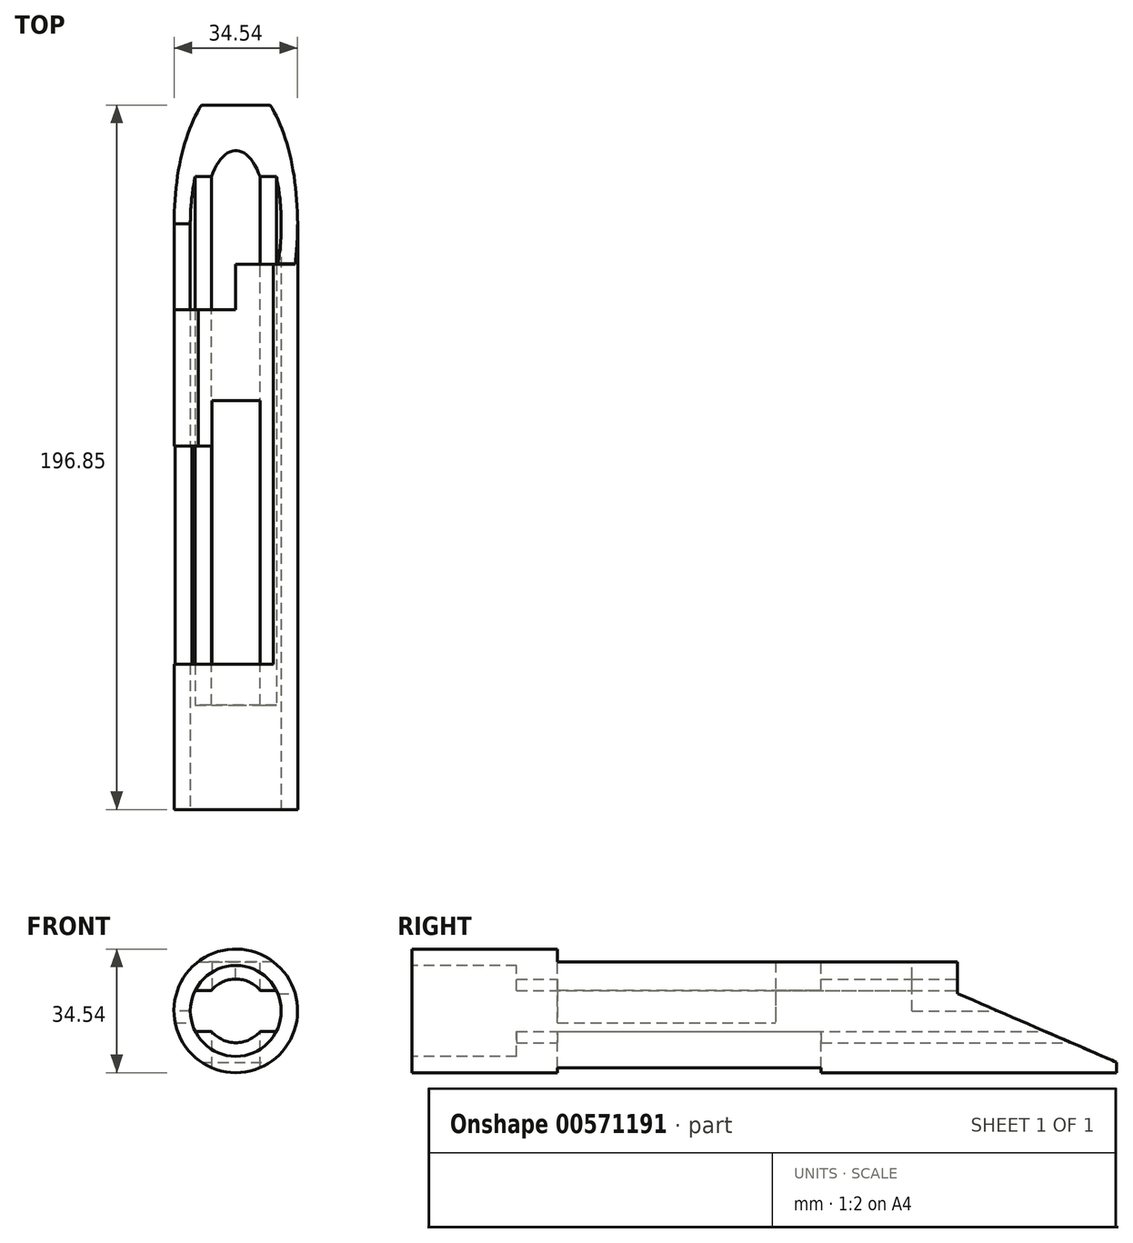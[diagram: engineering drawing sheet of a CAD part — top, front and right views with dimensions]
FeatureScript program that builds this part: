
annotation { "Feature Type Name" : "Feature", "Feature Type Description" : "" }
export const myFeature = defineFeature(function(context is Context, id is Id, definition is map)
    precondition{}
    {
        {
            var Q0;
            Q0=qCreatedBy(makeId("Front.planeOp"),FACE);
            var sketch = newSketch(context, id + "F0", { "sketchPlane" : qUnion([Q0])});
            skCircle(sketch, "E0", {"center": v(0, 0) * mm, "radius": 17.27 * mm});
            skCircle(sketch, "E1", {"center": v(0, 0) * mm, "radius": 8.89 * mm});
            skSolve(sketch);
        }
        {
            var Q0;
            Q0=qSketchRegion(id+"F0",true);
            extrude(context, id + "F1", {"entities" : qUnion([Q0]), "depth" : 196.85 * mm});
        }
        {
            var Q0;
            Q0=makeQuery(id+"F1.opExtrude","CAP_FACE",FACE,{"disambiguationData":[OSD([sQuery(id+"F0.wireOp",EDGE,"E0"),sQuery(id+"F0.wireOp",EDGE,"E1")])],"isStart":false});
            var sketch = newSketch(context, id + "F2", { "sketchPlane" : qUnion([Q0])});
            skCircle(sketch, "E2", {"center": v(0, 0) * mm, "radius": 12.7 * mm});
            skSolve(sketch);
        }
        {
            var Q0;
            Q0=qSketchRegion(id+"F2",true);
            extrude(context, id + "F3", {"entities" : qUnion([Q0]), "operationType" : NewBodyOperationType.REMOVE, "oppositeDirection" : true, "depth" : 29.2 * mm});
        }
        {
            var Q0;
            Q0=makeQuery(id+"F1.opExtrude","CAP_FACE",FACE,{"disambiguationData":[OSD([sQuery(id+"F0.wireOp",EDGE,"E0"),sQuery(id+"F0.wireOp",EDGE,"E1")])],"isStart":false});
            var sketch = newSketch(context, id + "F4", { "sketchPlane" : qUnion([Q0])});
            skArc(sketch, "E3", {"start": v(-11.34, 5.71) * mm, "mid": v(-12.7, 0) * mm, "end": v(-11.34, -5.71) * mm});
            skLineSegment(sketch, "E4", {"start": v(-11.34, 5.72) * mm, "end": v(11.34, 5.72) * mm});
            skLineSegment(sketch, "E5", {"start": v(-11.34, -5.72) * mm, "end": v(11.34, -5.72) * mm});
            skArc(sketch, "E6.trimOffspring", {"start": v(11.34, -5.71) * mm, "mid": v(12.7, 0) * mm, "end": v(11.34, 5.72) * mm});
            skSolve(sketch);
        }
        {
            var Q0;
            Q0=qSketchRegion(id+"F4",true);
            extrude(context, id + "F5", {"entities" : qUnion([Q0]), "operationType" : NewBodyOperationType.REMOVE, "endBound" : BoundingType.THROUGH_ALL, "oppositeDirection" : true, "depth" : 25.4 * mm});
        }
        {
            var Q0;
            Q0=qCreatedBy(makeId("Right.planeOp"),FACE);
            var sketch = newSketch(context, id + "F6", { "sketchPlane" : qUnion([Q0])});
            skLineSegment(sketch, "E7.bottom", {"start": v(-156.21, 26.76) * mm, "end": v(57.64, 26.76) * mm});
            skLineSegment(sketch, "E7.top", {"start": v(-156.21, 13.72) * mm, "end": v(57.64, 13.72) * mm});
            skLineSegment(sketch, "E7.left", {"start": v(-156.21, 26.76) * mm, "end": v(-156.21, 13.72) * mm});
            skLineSegment(sketch, "E7.right", {"start": v(57.64, 26.76) * mm, "end": v(57.64, 13.72) * mm});
            skSolve(sketch);
        }
        {
            var Q0;
            Q0=makeQuery(id+"F6.imprint","IMPRINT",FACE,{"disambiguationData":[TD([[makeQuery(id+"F6.imprint","IMPRINT",EDGE,{"derivedFrom":sQuery(id+"F6.wireOp",EDGE,"E7.bottom")}),-1.0]])]});
            extrude(context, id + "F7", {"entities" : qUnion([Q0]), "operationType" : NewBodyOperationType.REMOVE, "endBound" : BoundingType.THROUGH_ALL, "depth" : 25.4 * mm, "hasSecondDirection" : true, "secondDirectionBound" : SecondDirectionBoundingType.THROUGH_ALL, "secondDirectionOppositeDirection" : true, "secondDirectionDepth" : 25.4 * mm});
        }
        {
            var Q0;
            Q0=qCreatedBy(makeId("Right.planeOp"),FACE);
            var sketch = newSketch(context, id + "F8", { "sketchPlane" : qUnion([Q0])});
            skLineSegment(sketch, "E8.bottom", {"start": v(-57.15, 0) * mm, "end": v(7.94, 0) * mm});
            skLineSegment(sketch, "E8.top", {"start": v(-57.15, 18.94) * mm, "end": v(7.94, 18.94) * mm});
            skLineSegment(sketch, "E8.left", {"start": v(-57.15, 0) * mm, "end": v(-57.15, 18.94) * mm});
            skLineSegment(sketch, "E8.right", {"start": v(7.94, 0) * mm, "end": v(7.94, 18.94) * mm});
            skSolve(sketch);
        }
        {
            var Q0;
            Q0=makeQuery(id+"F8.imprint","IMPRINT",FACE,{"disambiguationData":[TD([[makeQuery(id+"F8.imprint","IMPRINT",EDGE,{"derivedFrom":sQuery(id+"F8.wireOp",EDGE,"E8.bottom")}),1.0]])]});
            extrude(context, id + "F9", {"entities" : qUnion([Q0]), "operationType" : NewBodyOperationType.REMOVE, "endBound" : BoundingType.THROUGH_ALL, "oppositeDirection" : true, "depth" : 25.4 * mm});
        }
        {
            var Q0;
            Q0=qCreatedBy(makeId("Right.planeOp"),FACE);
            var sketch = newSketch(context, id + "F10", { "sketchPlane" : qUnion([Q0])});
            skLineSegment(sketch, "E9.bottom", {"start": v(-44.45, 20.05) * mm, "end": v(14.07, 20.05) * mm});
            skLineSegment(sketch, "E9.top", {"start": v(-44.45, 4.83) * mm, "end": v(14.07, 4.83) * mm});
            skLineSegment(sketch, "E9.left", {"start": v(-44.45, 20.05) * mm, "end": v(-44.45, 4.83) * mm});
            skLineSegment(sketch, "E9.right", {"start": v(14.07, 20.05) * mm, "end": v(14.07, 4.83) * mm});
            skSolve(sketch);
        }
        {
            var Q0;
            Q0=makeQuery(id+"F10.imprint","IMPRINT",FACE,{"disambiguationData":[TD([[makeQuery(id+"F10.imprint","IMPRINT",EDGE,{"derivedFrom":sQuery(id+"F10.wireOp",EDGE,"E9.bottom")}),-1.0]])]});
            extrude(context, id + "F11", {"entities" : qUnion([Q0]), "operationType" : NewBodyOperationType.REMOVE, "endBound" : BoundingType.THROUGH_ALL, "depth" : 25.4 * mm});
        }
        {
            var Q0;
            Q0=qCreatedBy(makeId("Right.planeOp"),FACE);
            var sketch = newSketch(context, id + "F12", { "sketchPlane" : qUnion([Q0])});
            skLineSegment(sketch, "E10", {"start": v(-44.4, 4.81) * mm, "end": v(8.06, -17.87) * mm});
            skLineSegment(sketch, "E11", {"start": v(8.06, -17.87) * mm, "end": v(8.06, 8.4) * mm});
            skLineSegment(sketch, "E12", {"start": v(8.06, 8.4) * mm, "end": v(-43.8, 8.4) * mm});
            skLineSegment(sketch, "E13", {"start": v(-43.8, 8.4) * mm, "end": v(-44.4, 4.8) * mm});
            skSolve(sketch);
        }
        {
            var Q0;
            Q0=qSketchRegion(id+"F12",true);
            extrude(context, id + "F13", {"entities" : qUnion([Q0]), "operationType" : NewBodyOperationType.REMOVE, "endBound" : BoundingType.THROUGH_ALL, "oppositeDirection" : true, "depth" : 25.4 * mm, "hasSecondDirection" : true, "secondDirectionBound" : SecondDirectionBoundingType.THROUGH_ALL, "secondDirectionOppositeDirection" : false, "secondDirectionDepth" : 25.4 * mm});
        }
        {
            var Q0;
            Q0=qCreatedBy(makeId("Top.planeOp"),FACE);
            var sketch = newSketch(context, id + "F14", { "sketchPlane" : qUnion([Q0])});
            skLineSegment(sketch, "E14.bottom", {"start": v(-6.73, -156.21) * mm, "end": v(6.73, -156.21) * mm});
            skLineSegment(sketch, "E14.top", {"start": v(-6.73, -82.55) * mm, "end": v(6.73, -82.55) * mm});
            skLineSegment(sketch, "E14.left", {"start": v(-6.73, -156.21) * mm, "end": v(-6.73, -82.55) * mm});
            skLineSegment(sketch, "E14.right", {"start": v(6.73, -156.21) * mm, "end": v(6.73, -82.55) * mm});
            skPoint(sketch, "E14.middle", {"position": v(0, -119.38) * mm});
            skSolve(sketch);
        }
        {
            var Q0;
            Q0=qSketchRegion(id+"F14",true);
            extrude(context, id + "F15", {"entities" : qUnion([Q0]), "operationType" : NewBodyOperationType.REMOVE, "endBound" : BoundingType.THROUGH_ALL, "oppositeDirection" : true, "depth" : 25.4 * mm, "hasSecondDirection" : true, "secondDirectionBound" : SecondDirectionBoundingType.THROUGH_ALL, "secondDirectionOppositeDirection" : false, "secondDirectionDepth" : 25.4 * mm});
        }
        {
            var Q0;
            Q0=qCreatedBy(makeId("Right.planeOp"),FACE);
            var sketch = newSketch(context, id + "F16", { "sketchPlane" : qUnion([Q0])});
            skLineSegment(sketch, "E15.bottom", {"start": v(-156.21, 18.6) * mm, "end": v(-95.25, 18.6) * mm});
            skLineSegment(sketch, "E15.top", {"start": v(-156.21, -3.34) * mm, "end": v(-95.25, -3.34) * mm});
            skLineSegment(sketch, "E15.left", {"start": v(-156.21, 18.6) * mm, "end": v(-156.21, -3.34) * mm});
            skLineSegment(sketch, "E15.right", {"start": v(-95.25, 18.6) * mm, "end": v(-95.25, -3.34) * mm});
            skSolve(sketch);
        }
        {
            var Q0;
            Q0=qSketchRegion(id+"F16",true);
            extrude(context, id + "F17", {"entities" : qUnion([Q0]), "operationType" : NewBodyOperationType.REMOVE, "endBound" : BoundingType.THROUGH_ALL, "oppositeDirection" : true, "depth" : 25.4 * mm});
        }
    });
